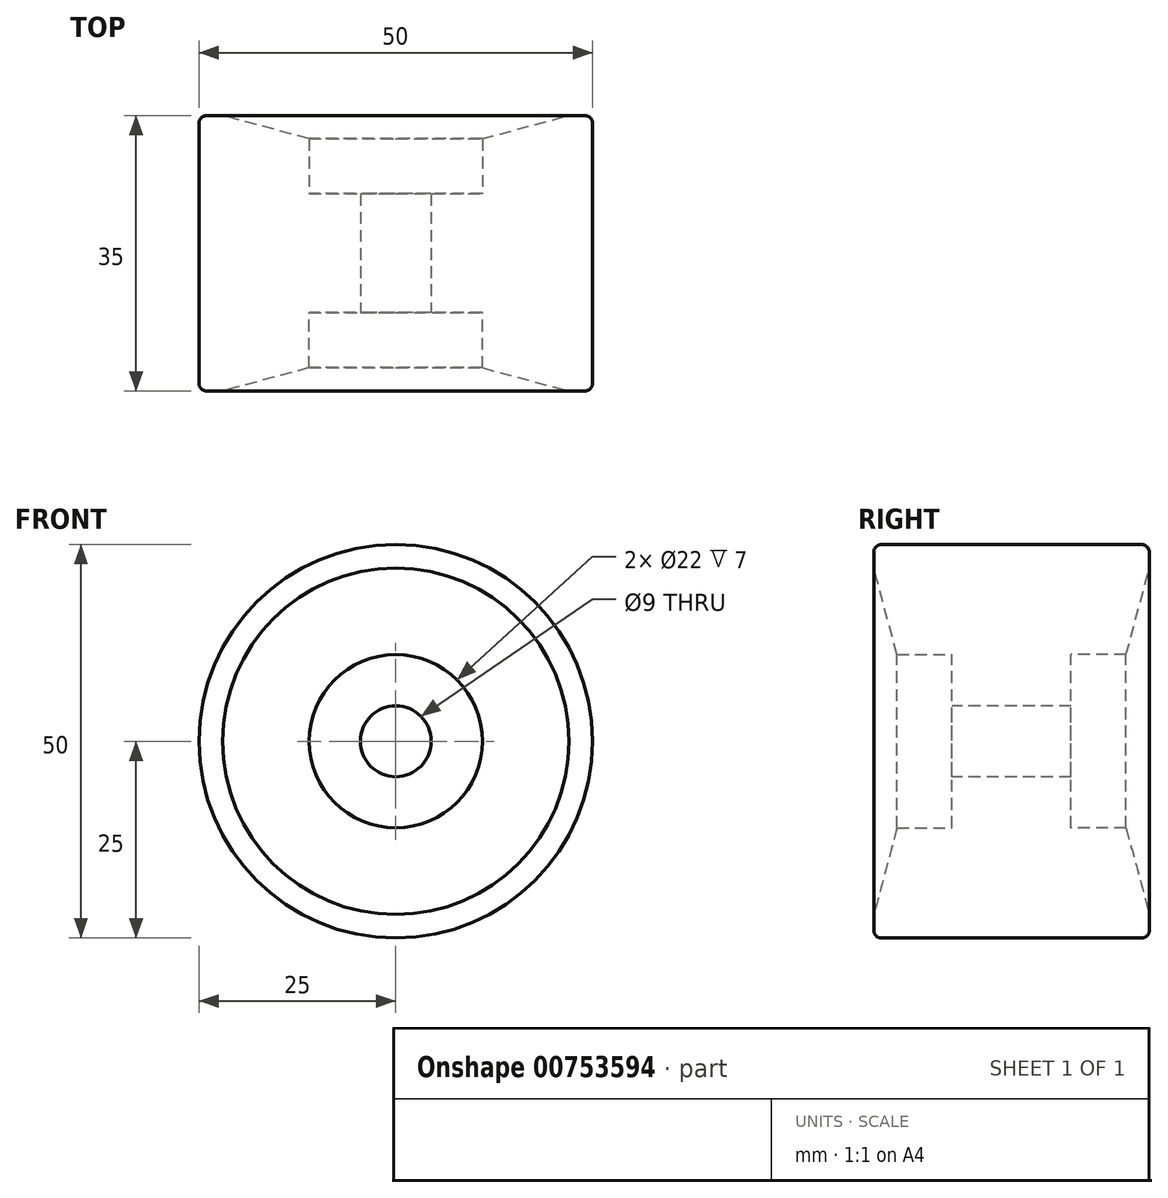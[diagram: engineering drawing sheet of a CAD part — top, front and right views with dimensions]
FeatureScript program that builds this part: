
annotation { "Feature Type Name" : "Feature", "Feature Type Description" : "" }
export const myFeature = defineFeature(function(context is Context, id is Id, definition is map)
    precondition{}
    {
        {
            var Q0;
            Q0=qCreatedBy(makeId("Right.planeOp"),FACE);
            var sketch = newSketch(context, id + "F0", { "sketchPlane" : qUnion([Q0])});
            skLineSegment(sketch, "E0", {"start": v(0, 4.5) * mm, "end": v(0, 25) * mm});
            skLineSegment(sketch, "E1", {"start": v(0, 25) * mm, "end": v(16.5, 25) * mm});
            skLineSegment(sketch, "E2", {"start": v(0, 0) * mm, "end": v(7.55, 0) * mm});
            skLineSegment(sketch, "E3", {"start": v(7.55, 4.5) * mm, "end": v(7.55, 11) * mm});
            skLineSegment(sketch, "E4", {"start": v(7.55, 11) * mm, "end": v(14.55, 11) * mm});
            skLineSegment(sketch, "E5", {"start": v(0, 4.5) * mm, "end": v(7.55, 4.5) * mm});
            skLineSegment(sketch, "E6", {"start": v(17.5, 24) * mm, "end": v(17.5, 22) * mm});
            skLineSegment(sketch, "E7", {"start": v(17.5, 22) * mm, "end": v(14.55, 11) * mm});
            skPoint(sketch, "E8.visualSharp", {"position": v(17.5, 25) * mm});
            skArc(sketch, "E8.filletArc", {"start": v(17.5, 24) * mm, "mid": v(17.2, 24.7) * mm, "end": v(16.5, 25) * mm});
            skSolve(sketch);
        }
        {
            var Q0;
            Q0 = qSketchRegion(id + "F0", true);
            var Q1;
            Q1=sQuery(id+"F0.wireOp",EDGE,"E2");
            revolve(context, id + "F1", {"surfaceOperationType" : NewSurfaceOperationType.NEW, "entities" : qUnion([Q0]), "axis" : qUnion([Q1]), "revolveType" : RevolveType.FULL});
        }
        {
            var Q0;
            Q0=makeQuery(id+"F1.opRevolve","SWEPT_BODY",BODY,{"disambiguationData":[OSD([sQuery(id+"F0.wireOp",EDGE,"E0"),sQuery(id+"F0.wireOp",EDGE,"E1"),sQuery(id+"F0.wireOp",EDGE,"E3"),sQuery(id+"F0.wireOp",EDGE,"E4"),sQuery(id+"F0.wireOp",EDGE,"E5"),sQuery(id+"F0.wireOp",EDGE,"E6"),sQuery(id+"F0.wireOp",EDGE,"E7"),sQuery(id+"F0.wireOp",EDGE,"E8.filletArc")])]});
            var Q1;
            Q1=makeQuery(id+"F1.opRevolve","SWEPT_FACE",FACE,{"disambiguationData":[OSD([sQuery(id+"F0.wireOp",EDGE,"E0")])]});
            mirror(context, id + "F2", {"operationType" : NewBodyOperationType.ADD, "entities" : qUnion([Q0]), "mirrorPlane" : qUnion([Q1])});
        }
    });
